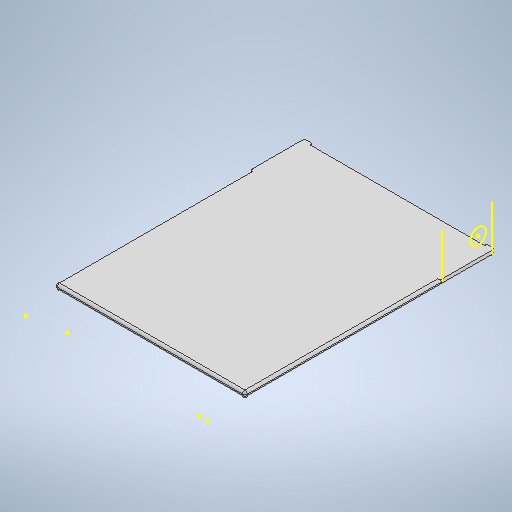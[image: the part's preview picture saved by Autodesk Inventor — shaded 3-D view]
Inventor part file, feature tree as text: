
AUTODESK INVENTOR PART (.ipt)
format: ipt  version: 2025.2 (Build 292293000, 293)  size: 361,984 bytes
history: native  units: in
note: dims shown in document units (in); Inventor stores cm internally (conversion verified against a paired STEP export)
features: sketch x11, thread x10, extrude x9, fillet x3
ambient origin geometry x8: Origin, YZ Plane, XZ Plane, XY Plane, X Axis, Y Axis, Z Axis, Center Point
bodies: Body1 (feature_tree)
feature tree (33):
  sketch  "Sketch1"  dims[d0=6.2992in d1=8.2677in]
  extrude  "Extrusion3"  Depth=8.2677in
  sketch  "Sketch2"  dims[d12=0.1969in d13=0.0in d14=0.2756in]
  extrude  "Extrusion4"  Depth=0.1969in
  sketch  "Sketch3"  dims[d15=1.811in d16=0.2756in]
  sketch  "Sketch5"  dims[d17=1.811in d18=1.6535in d19=0.0in]
  sketch  "Sketch6"  dims[d28=0.3937in d29=0.0in d47=0.1181in d48=0.3937in d49=0.0in d50=0.3937in d51=0.0in d62=0.2756in d63=0.0in d64=0.2756in d65=0.0in d66=0.2756in d67=0.0in d68=0.2756in d69=0.0in d70=0.0787in d72=0.2657in d73=0.2657in d75=0.0in d76=0.3937in d77=0.1181in d79=0.0in d80=0.3937in d81=0.1181in d83=0.0in d84=0.3937in d85=0.2756in d86=0.0in d87=0.2756in d88=0.0in]
  extrude  "Extrusion6"  Depth=0.2756in
  sketch  "Sketch8"  dims[d89=0.2756in d90=0.0in d91=0.2756in d92=0.0in]
  extrude  "Extrusion7"  Depth=1.6535in TaperAngle=0.0deg
  extrude  "Extrusion8"  Depth=0.3937in
  thread  "Thread5"  [1 undecoded]
  thread  "Thread6"  [1 undecoded]
  thread  "Thread7"  [1 undecoded]
  thread  "Thread8"  [1 undecoded]
  fillet  "Fillet1"  Radius=0.2756in
  sketch  "Sketch9"  dims[d93=0.2756in d94=0.0in d95=0.2756in d96=0.0in]
  thread  "Thread9"  [1 undecoded]
  thread  "Thread10"  [1 undecoded]
  thread  "Thread11"  [1 undecoded]
  thread  "Thread12"  [1 undecoded]
  thread  "Thread13"  [1 undecoded]
  thread  "Thread14"  [1 undecoded]
  fillet  "Fillet2"  Radius=0.2756in
  fillet  "Fillet3"  Radius=0.2756in
  extrude  "Extrusion13"  Depth=0.2756in TaperAngle=0.0deg
  sketch  "Sketch13"  dims[d8=0.0197in d9=0.0344in d20=0.0197in d21=0.0344in d22=0.0197in d23=0.0344in d52=0.0197in d53=0.0344in d54=0.0197in d55=0.0344in]
  sketch  "Sketch10"  dims[d97=0.0787in d98=0.0787in]
  sketch  "Sketch11"  dims[d99=43744.5276in d100=0.0in d6=0.0197in]
  sketch  "Sketch12"  dims[d7=0.0344in]
  extrude  "Extrusion10"  Depth=0.2756in TaperAngle=0.0deg
  extrude  "Extrusion11"  Depth=0.0787in
  extrude  "Extrusion12"  Depth=0.0197in
note: 10 required parameter values undecoded (feature->parameter linkage not recoverable at this tier; creation-order binding heuristic only, values carry confidence <= 0.55)
